# Revit family: FP_Revit_18_OR90SCI1X1_Range_90001034A
name_source: partatom
category: Specialty Equipment
revit_build: Autodesk Revit 2018 (Build: 20170223_1515(x64)
units: mm (PartAtom-declared; Revit-internal decimal feet)

## family parameters
Always vertical = Yes
Cut with Voids When Loaded = Yes
OmniClass Number = 23.40.40.14.17.17
OmniClass Title = Ranges
Part Type = Normal
Room Calculation Point = No
Round Connector Dimension = Use Diameter
Shared = No
Work Plane-Based = No

## types (1)
- FP_Revit_18_OR90SCI1X1_Range_90001034A
    Cavity - Depth = 600 mm  [stored 1.9685 ft]
    Cavity - Height = 915 mm  [stored 3.00197 ft]
    Cavity - Width = 900 mm  [stored 2.95276 ft]
    Chassis - Depth = 594 mm
    Chassis - Height = 814 mm
    Chassis - Width = 897 mm  [stored 2.94291 ft]
    Clearance - Overhead Combustible = 650 mm  [stored 2.13255 ft]
    Clearance - Overhead Non-Combustible = 450 mm  [stored 1.47638 ft]
    Clearance - Overhead Rangehood = 650 mm  [stored 2.13255 ft]
    Clearance - Rear Combustible = 0 mm  [stored 0 ft]
    Clearance - Rear Non-Combustible = 0 mm  [stored 0 ft]
    Clearance - Side Combustible = 50 mm  [stored 0.164042 ft]
    Clearance - Side Non-Combustible = 0 mm  [stored 0 ft]
    Connector Description - Electrical = 220-240 V, 50 Hz, 46.1 A
    Countertop Height (min 908mm - max 933mm) = 915 mm  [stored 3.00197 ft]
    Description = 90cm Classic Freestanding Cooker (Stainless)
    Manufacturer = Fisher & Paykel Appliances
    Material - Body = Fisher & Paykel - Stainless Steel
    Material - Buttons and Dials = Fisher & Paykel - Steel, Chrome Plated
    Material - Cooktop = Fisher & Paykel - Black
    Material - Door Front = Fisher & Paykel - Stainless Steel
    Material - Handle = Fisher & Paykel - Aluminium
    Material - Trim = Fisher & Paykel - Steel, Chrome Plated
    Model = OR90SCI1X1
    Optional - Toe Kick Panel = KICKOR90X1
    Product - Depth = 641 mm
    Product - Height = 915 mm  [stored 3.00197 ft]
    Product - Width = 897 mm  [stored 2.94291 ft]
    URL = www.fisherpaykel.com
    Visibility - Adjustable Feet Covers = Yes
    Visibility - Clearance Required = Yes
    Visibility - Rear Trim (Supplied) = Yes
    Visibility - Toe Kick Panel (Optional) = No

note: [stored X ft] marks values corroborated as IEEE doubles in the binary element streams (Revit-internal decimal feet)

## geometry (parser evidence)
native form markers: Sweep x15
no freeform markers — native parametric forms only
